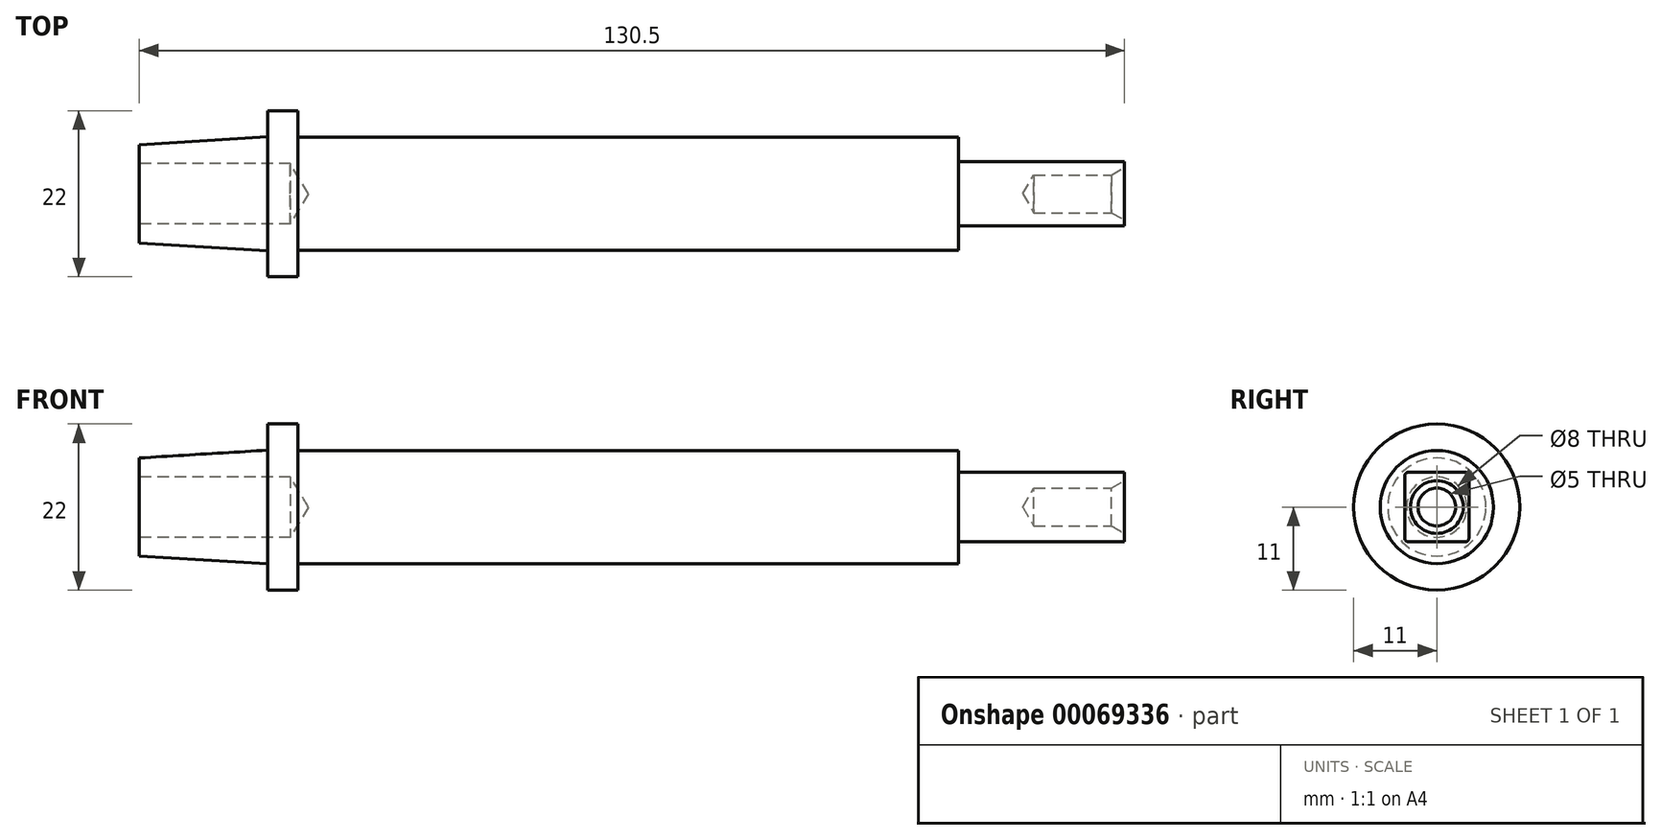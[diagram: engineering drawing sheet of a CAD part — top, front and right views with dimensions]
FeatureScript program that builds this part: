
annotation { "Feature Type Name" : "Feature", "Feature Type Description" : "" }
export const myFeature = defineFeature(function(context is Context, id is Id, definition is map)
    precondition{}
    {
        {
            var Q0;
            Q0=qCreatedBy(makeId("Front.planeOp"),FACE);
            var sketch = newSketch(context, id + "F0", { "sketchPlane" : qUnion([Q0])});
            skLineSegment(sketch, "E0", {"start": v(-21, 0) * mm, "end": v(-21, 6.5) * mm});
            skLineSegment(sketch, "E1", {"start": v(-21, 6.5) * mm, "end": v(-4, 7.54) * mm});
            skLineSegment(sketch, "E2", {"start": v(-4, 7.54) * mm, "end": v(-4, 11) * mm});
            skLineSegment(sketch, "E3", {"start": v(-4, 11) * mm, "end": v(0, 11) * mm});
            skLineSegment(sketch, "E4", {"start": v(0, 11) * mm, "end": v(0, 7.5) * mm});
            skLineSegment(sketch, "E5", {"start": v(0, 7.5) * mm, "end": v(87.5, 7.5) * mm});
            skLineSegment(sketch, "E6", {"start": v(87.5, 0) * mm, "end": v(87.5, 7.5) * mm});
            skLineSegment(sketch, "E7", {"start": v(-21, 0) * mm, "end": v(87.5, 0) * mm});
            skSolve(sketch);
        }
        {
            var Q0;
            Q0 = qSketchRegion(id + "F0", true);
            var Q1;
            Q1=sQuery(id+"F0.wireOp",EDGE,"E7");
            revolve(context, id + "F1", {"entities" : qUnion([Q0]), "axis" : qUnion([Q1]), "revolveType" : RevolveType.FULL});
        }
        {
            var Q0;
            Q0=makeQuery(id+"F1.opRevolve","SWEPT_FACE",FACE,{"disambiguationData":[OSD([sQuery(id+"F0.wireOp",EDGE,"E6")])]});
            var sketch = newSketch(context, id + "F2", { "sketchPlane" : qUnion([Q0])});
            skLineSegment(sketch, "E8.rect.bottom", {"start": v(4.25, 4.62) * mm, "end": v(-4.25, 4.62) * mm});
            skLineSegment(sketch, "E8.rect.top", {"start": v(4.25, -4.62) * mm, "end": v(-4.25, -4.62) * mm});
            skLineSegment(sketch, "E8.rect.left", {"start": v(4.25, 4.62) * mm, "end": v(4.25, -4.62) * mm});
            skLineSegment(sketch, "E8.rect.right", {"start": v(-4.25, 4.62) * mm, "end": v(-4.25, -4.62) * mm});
            skPoint(sketch, "E8.rect.middle", {"position": v(0, 0) * mm});
            skSolve(sketch);
        }
        {
            var Q0;
            Q0=makeQuery(id+"F2.imprint","IMPRINT",FACE,{"disambiguationData":[TD([[makeQuery(id+"F2.imprint","IMPRINT",EDGE,{"derivedFrom":sQuery(id+"F2.wireOp",EDGE,"E8.rect.bottom")}),1.0]])]});
            extrude(context, id + "F3", {"entities" : qUnion([Q0]), "operationType" : NewBodyOperationType.ADD, "depth" : 22 * mm});
        }
        {
            var Q0;
            Q0=makeQuery(id+"F1.opRevolve","SWEPT_FACE",FACE,{"disambiguationData":[OSD([sQuery(id+"F0.wireOp",EDGE,"E0")])]});
            var sketch = newSketch(context, id + "F4", { "sketchPlane" : qUnion([Q0])});
            skPoint(sketch, "E9", {"position": v(0, 0) * mm});
            skSolve(sketch);
        }
        {
            var Q0;
            Q0=sQuery(id+"F4.wireOp",VERTEX,"E9");
            var Q1;
            Q1=makeQuery(id+"F1.opRevolve","SWEPT_BODY",BODY,{"disambiguationData":[OSD([sQuery(id+"F0.wireOp",EDGE,"E0"),sQuery(id+"F0.wireOp",EDGE,"E1"),sQuery(id+"F0.wireOp",EDGE,"E2"),sQuery(id+"F0.wireOp",EDGE,"E3"),sQuery(id+"F0.wireOp",EDGE,"E4"),sQuery(id+"F0.wireOp",EDGE,"E5"),sQuery(id+"F0.wireOp",EDGE,"E6"),sQuery(id+"F0.wireOp",EDGE,"E7")])]});
            hole(context, id + "F5", {"style" : HoleStyle.SIMPLE, "holeDiameter" : 8 * mm, "endStyle" : HoleEndStyle.BLIND, "holeDepth" : 20 * mm, "locations" : qUnion([Q0]), "scope" : qUnion([Q1])});
        }
        {
            var Q0;
            Q0=makeQuery(id+"F3.opExtrude","SWEPT_EDGE",EDGE,{"disambiguationData":[OSD([sQuery(id+"F2.wireOp",EDGE,"E8.rect.bottom"),sQuery(id+"F2.wireOp",EDGE,"E8.rect.right")])]});
            var Q1;
            Q1=makeQuery(id+"F3.opExtrude","SWEPT_EDGE",EDGE,{"disambiguationData":[OSD([sQuery(id+"F2.wireOp",EDGE,"E8.rect.top"),sQuery(id+"F2.wireOp",EDGE,"E8.rect.right")])]});
            var Q2;
            Q2=makeQuery(id+"F3.opExtrude","SWEPT_EDGE",EDGE,{"disambiguationData":[OSD([sQuery(id+"F2.wireOp",EDGE,"E8.rect.bottom"),sQuery(id+"F2.wireOp",EDGE,"E8.rect.left")])]});
            var Q3;
            Q3=makeQuery(id+"F3.opExtrude","SWEPT_EDGE",EDGE,{"disambiguationData":[OSD([sQuery(id+"F2.wireOp",EDGE,"E8.rect.top"),sQuery(id+"F2.wireOp",EDGE,"E8.rect.left")])]});
            fillet(context, id + "F6", {"entities" : qUnion([Q0, Q1, Q2, Q3]), "radius" : .5 * mm, "tangentPropagation" : true, "allowEdgeOverflow" : false});
        }
        {
            var Q0;
            Q0=makeQuery(id+"F3.opExtrude","CAP_FACE",FACE,{"disambiguationData":[OSD([sQuery(id+"F2.wireOp",EDGE,"E8.rect.bottom"),sQuery(id+"F2.wireOp",EDGE,"E8.rect.top"),sQuery(id+"F2.wireOp",EDGE,"E8.rect.left"),sQuery(id+"F2.wireOp",EDGE,"E8.rect.right")])],"isStart":false});
            var sketch = newSketch(context, id + "F7", { "sketchPlane" : qUnion([Q0])});
            skPoint(sketch, "E10", {"position": v(0, 0) * mm});
            skSolve(sketch);
        }
        {
            var Q0;
            Q0=sQuery(id+"F7.wireOp",VERTEX,"E10");
            var Q1;
            Q1=makeQuery(id+"F1.opRevolve","SWEPT_BODY",BODY,{"disambiguationData":[OSD([sQuery(id+"F0.wireOp",EDGE,"E0"),sQuery(id+"F0.wireOp",EDGE,"E1"),sQuery(id+"F0.wireOp",EDGE,"E2"),sQuery(id+"F0.wireOp",EDGE,"E3"),sQuery(id+"F0.wireOp",EDGE,"E4"),sQuery(id+"F0.wireOp",EDGE,"E5"),sQuery(id+"F0.wireOp",EDGE,"E6"),sQuery(id+"F0.wireOp",EDGE,"E7")])]});
            hole(context, id + "F8", {"style" : HoleStyle.C_SINK, "endStyle" : HoleEndStyle.BLIND, "holeDiameter" : 5 * mm, "cSinkDiameter" : 7 * mm, "cSinkAngle" : 60 * degree, "majorDiameter" : 5 * mm, "holeDepth" : 12 * mm, "isTappedThrough" : true, "tappedDepth" : 12 * mm, "tapClearance" : 3, "locations" : qUnion([Q0]), "scope" : qUnion([Q1])});
        }
    });
